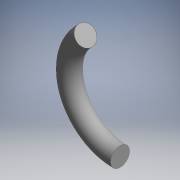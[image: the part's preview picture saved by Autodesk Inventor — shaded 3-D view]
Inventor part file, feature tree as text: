
AUTODESK INVENTOR PART (.ipt)
format: ipt  version: 2018 (Build 220112000, 112)  size: 126,976 bytes
history: native  units: in
note: dims shown in document units (in); Inventor stores cm internally (conversion verified against a paired STEP export)
features: sweep x3
ambient origin geometry x8: Origin, YZ Plane, XZ Plane, XY Plane, X Axis, Y Axis, Z Axis, Center Point
bodies: Solid1 (feature_tree)
feature tree (3):
  sweep  "Ring"
  sweep  "Sweep Path"
  sweep  "Sweep Profile"
